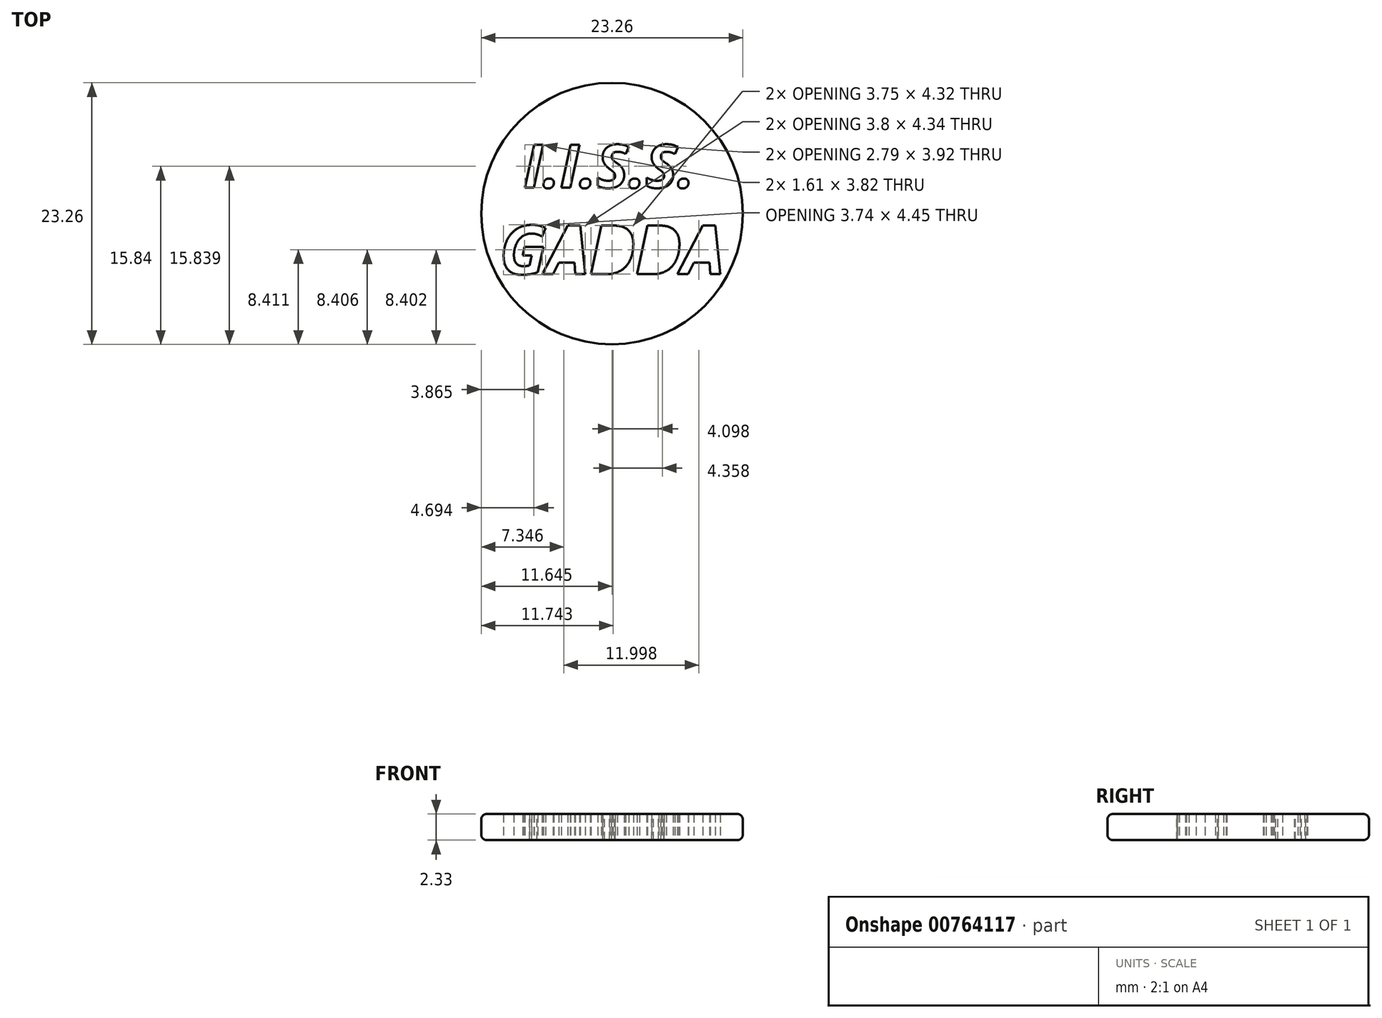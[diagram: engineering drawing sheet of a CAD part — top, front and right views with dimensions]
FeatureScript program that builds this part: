
annotation { "Feature Type Name" : "Feature", "Feature Type Description" : "" }
export const myFeature = defineFeature(function(context is Context, id is Id, definition is map)
    precondition{}
    {
        {
            var Q0;
            Q0=qCreatedBy(makeId("Top.planeOp"),FACE);
            var sketch = newSketch(context, id + "F0", { "sketchPlane" : qUnion([Q0])});
            skCircle(sketch, "E0", {"center": v(0, 0) * mm, "radius": 11.62 * mm});
            skText(sketch, "E1", { "text": "GADDA", "fontName": "NotoSans-BoldItalic.ttf"});
            skText(sketch, "E2", { "text": "I.I.S.S.", "fontName": "OpenSans-BoldItalic.ttf"});
            const initialGuessF0  = {"E1": [-0.01, -0.00539, 1, 0, 0.00436], "E2": [-0.00788, 0.0023, 1, 0, 0.00385]};
            skSetInitialGuess(sketch, initialGuessF0);
            skSolve(sketch);
        }
        {
            var Q0;
            Q0=makeQuery(id+"F0.imprint","IMPRINT",FACE,{"disambiguationData":[TD([[makeQuery(id+"F0.imprint","IMPRINT",EDGE,{"derivedFrom":sQuery(id+"F0.wireOp",EDGE,"E0")}),1.0]])]});
            extrude(context, id + "F1", {"entities" : qUnion([Q0]), "depth" : 2.33 * mm, "offsetDistance" : 25 * mm});
        }
        {
            var Q0;
            Q0=makeQuery(id+"F1.opExtrude","CAP_EDGE",EDGE,{"disambiguationData":[OSD([sQuery(id+"F0.wireOp",EDGE,"E0")])],"isStart":false});
            var Q1;
            Q1=makeQuery(id+"F1.opExtrude","CAP_EDGE",EDGE,{"disambiguationData":[OSD([sQuery(id+"F0.wireOp",EDGE,"E0")])],"isStart":true});
            fillet(context, id + "F2", {"entities" : qUnion([Q0, Q1]), "radius" : 0.5 * mm, "tangentPropagation" : true, "allowEdgeOverflow" : false});
        }
    });
